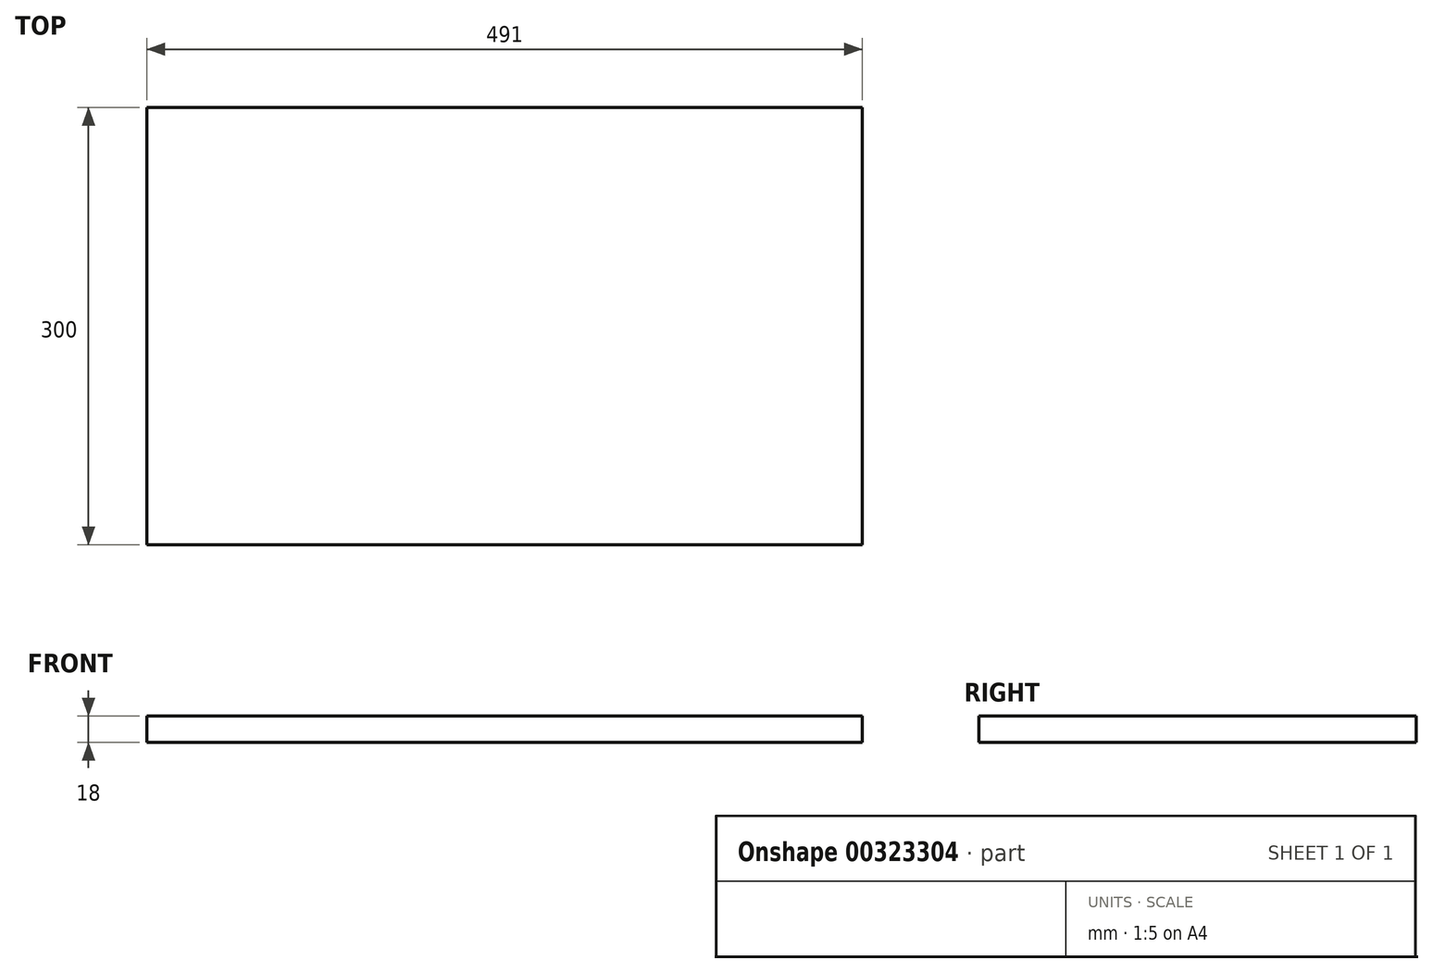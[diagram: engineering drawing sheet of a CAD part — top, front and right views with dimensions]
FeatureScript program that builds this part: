
annotation { "Feature Type Name" : "Feature", "Feature Type Description" : "" }
export const myFeature = defineFeature(function(context is Context, id is Id, definition is map)
    precondition{}
    {
        {
            var Q0;
            Q0=qCreatedBy(makeId("Top.planeOp"),FACE);
            var sketch = newSketch(context, id + "F0", { "sketchPlane" : qUnion([Q0])});
            skLineSegment(sketch, "E0.bottom", {"start": v(0, 0) * mm, "end": v(491, 0) * mm});
            skLineSegment(sketch, "E0.top", {"start": v(0, 300) * mm, "end": v(491, 300) * mm});
            skLineSegment(sketch, "E0.left", {"start": v(0, 0) * mm, "end": v(0, 300) * mm});
            skLineSegment(sketch, "E0.right", {"start": v(491, 0) * mm, "end": v(491, 300) * mm});
            skSolve(sketch);
        }
        {
            var Q0;
            Q0 = qSketchRegion(id + "F0", true);
            extrude(context, id + "F1", {"entities" : qUnion([Q0]), "depth" : 18 * mm, "offsetDistance" : 25 * mm});
        }
    });
